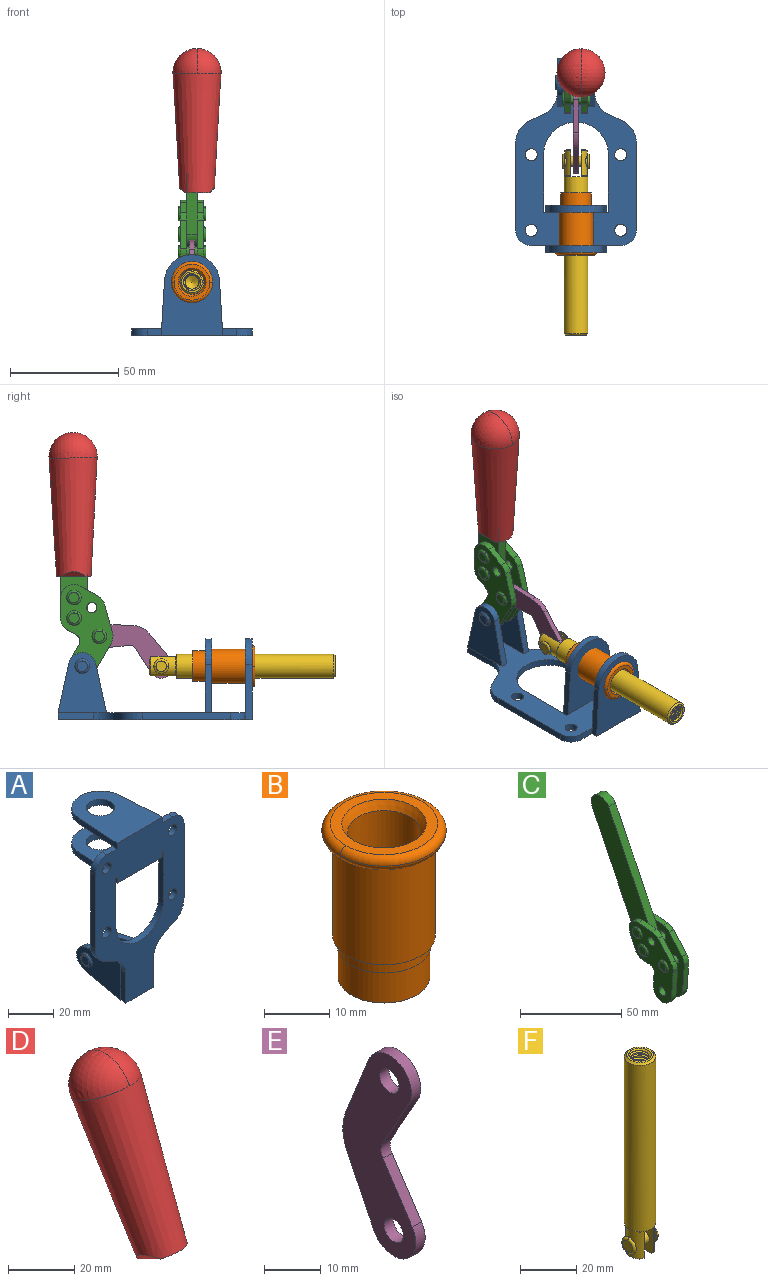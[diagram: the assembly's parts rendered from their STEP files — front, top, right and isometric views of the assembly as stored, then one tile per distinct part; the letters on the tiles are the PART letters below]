
ASSEMBLY  parts=6 mates=6
PART A: 55 faces, bbox 55.7x37.4x89.8 mm
  f0: torus R=2.41mm, axis (-1,0,0), area 15mm2, adj f11,f15,f25
  f1: torus R=2.41mm, axis (-1,0,0), area 15mm2, adj f10,f12,f22
  f2: cylinder r=2.78mm len=5.56mm, axis (0,-1,0), area 54.2mm2, adj f30,f54
  f3: cylinder r=14.99mm len=29.97mm, axis (0,-1,0), area 145.9mm2, adj f30,f49,f53,f54
  f4: cylinder r=2.78mm len=5.56mm, axis (0,-1,0), area 54.2mm2, adj f30,f54
  f5: cylinder r=2.78mm len=5.56mm, axis (0,-1,0), area 54.2mm2, adj f30,f54
  f6: cylinder r=2.78mm len=5.56mm, axis (0,-1,0), area 54.2mm2, adj f30,f54
  f7: cylinder r=6.35mm len=12.7mm, axis (0,0,1), area 123.6mm2, adj f27,f51
  f8: cylinder r=6.35mm len=12.7mm, axis (0,0,-1), area 124.7mm2, adj f21,f35
  f9: cylinder r=2.41mm len=11.18mm, axis (-1,0,0), area 169.4mm2, adj f16,f19
  f10: plane 4.83x4.83mm, normal (1,0,0), area 18.3mm2, adj f1,f12
  f11: plane 4.83x4.83mm, normal (-1,0,0), area 18.3mm2, adj f0,f15
  f12: torus R=2.41mm, axis (-1,0,0), area 15mm2, adj f1,f10,f22
  f13: cylinder r=6.35mm len=12.41mm, axis (1,0,0), area 53.4mm2, adj f18,f19,f22,f23
  f14: cylinder r=6.35mm len=12.41mm, axis (-1,0,0), area 53.4mm2, adj f16,f17,f24,f25
  f15: torus R=2.41mm, axis (-1,0,0), area 15mm2, adj f0,f11,f25
  f16: plane 27.86x22.35mm, normal (1,0,0), area 425.4mm2, adj f9,f14,f17,f24,f30
  f17: plane 22.86x4.97mm, normal (0,0.21,0.98), area 72.5mm2, adj f14,f16,f25,f30
  f18: plane 22.86x4.97mm, normal (0,0.21,0.98), area 72.5mm2, adj f13,f19,f22,f30
  f19: plane 27.86x22.35mm, normal (-1,0,0), area 425.4mm2, adj f9,f13,f18,f23,f30
  f20: cylinder r=12.7mm len=25.35mm, axis (0,0,-1), area 119.8mm2, adj f21,f34,f35,f36
  f21: plane 34.21x28.07mm, normal (0,0,-1), area 702.4mm2, adj f8,f20,f30,f34,f36
  f22: plane 27.96x22.45mm, normal (1,0,0), area 407.2mm2, adj f1,f12,f13,f18,f23,f30,f42,f43
  f23: plane 22.86x4.97mm, normal (0,0.21,-0.98), area 72.5mm2, adj f13,f19,f22,f44
  f24: plane 22.86x4.97mm, normal (0,0.21,-0.98), area 72.5mm2, adj f14,f16,f25,f44
  f25: plane 27.86x22.35mm, normal (-1,0,0), area 407.1mm2, adj f0,f14,f15,f17,f24,f30,f45,f46
  f26: plane 3.1x0.95mm, normal (0,0,-1), area 2.7mm2, adj f30,f49,f50,f54
  f27: plane 34.21x28.07mm, normal (0,0,1), area 702.4mm2, adj f7,f28,f30,f50,f52
  f28: cylinder r=12.7mm len=25.35mm, axis (0,0,1), area 118.8mm2, adj f27,f50,f51,f52
  f29: plane 3.1x0.95mm, normal (0,0,-1), area 2.7mm2, adj f30,f52,f53,f54
  f30: plane 86.54x55.63mm, normal (0,1,0), area 2362.9mm2, adj f2,f3,f4,f5,f6,f16,f17,f18
  f31: plane 40.56x3.1mm, normal (-1,0,0), area 125.7mm2, adj f30,f32,f48,f54
  f32: cylinder r=7.11mm len=7.11mm, axis (0,-1,0), area 34.6mm2, adj f30,f31,f33,f54
  f33: plane 6.67x3.1mm, normal (0,0,1), area 20.4mm2, adj f30,f32,f34,f54
  f34: plane 25.39x3.13mm, normal (-1,0.06,0), area 79.5mm2, adj f20,f21,f33,f35,f54
  f35: plane 37.31x28.45mm, normal (0,0,1), area 789.9mm2, adj f8,f20,f34,f36,f54
  f36: plane 25.39x3.13mm, normal (1,0.06,0), area 79.5mm2, adj f20,f21,f35,f37,f54
  f37: plane 6.67x3.1mm, normal (0,0,1), area 20.4mm2, adj f30,f36,f38,f54
  f38: cylinder r=7.11mm len=7.11mm, axis (0,-1,0), area 34.6mm2, adj f30,f37,f39,f54
  f39: plane 40.56x3.1mm, normal (1,0,0), area 125.7mm2, adj f30,f38,f40,f54
  f40: cylinder r=11.18mm len=10.16mm, axis (0,-1,0), area 39.5mm2, adj f30,f39,f41,f54
  f41: plane 6.09x3.1mm, normal (0.42,0,-0.91), area 20.8mm2, adj f30,f40,f42,f54
  f42: cylinder r=11.18mm len=9.41mm, axis (0,-1,0), area 37.2mm2, adj f22,f30,f41,f43,f54
  f43: plane 16.5x3.1mm, normal (1,0,0), area 51.1mm2, adj f22,f42,f44,f54
  f44: plane 17.37x3.1mm, normal (0,0,-1), area 53.8mm2, adj f23,f24,f30,f43,f45,f54
  f45: plane 16.5x3.1mm, normal (-1,0,0), area 51.1mm2, adj f25,f44,f46,f54
  f46: cylinder r=11.18mm len=9.41mm, axis (0,-1,0), area 37.2mm2, adj f25,f30,f45,f47,f54
  f47: plane 6.09x3.1mm, normal (-0.42,0,-0.91), area 20.8mm2, adj f30,f46,f48,f54
  f48: cylinder r=11.18mm len=10.16mm, axis (0,-1,0), area 39.5mm2, adj f30,f31,f47,f54
  f49: plane 26.54x3.1mm, normal (-1,0,0), area 82.3mm2, adj f3,f26,f30,f54
  f50: plane 25.39x3.1mm, normal (1,0.06,0), area 78.8mm2, adj f26,f27,f28,f51,f54
  f51: plane 37.31x28.45mm, normal (0,0,-1), area 789.9mm2, adj f7,f28,f50,f52,f54
  f52: plane 25.39x3.1mm, normal (-1,0.06,0), area 78.8mm2, adj f27,f28,f29,f51,f54
  f53: plane 26.54x3.1mm, normal (1,0,0), area 82.3mm2, adj f3,f29,f30,f54
  f54: plane 89.66x55.63mm, normal (0,-1,0), area 2678.5mm2, adj f2,f3,f4,f5,f6,f26,f29,f31
PART B: 15 faces, bbox 20.6x20.6x28.7 mm
  f0: torus R=8.26mm, axis (0,0,1), area 56.8mm2, adj f1,f10,f12
  f1: torus R=8.26mm, axis (0,0,1), area 56.8mm2, adj f0,f6,f13
  f2: cylinder r=5.59mm len=25.91mm, axis (0,0,1), area 909.6mm2, adj f3,f4
  f3: cone r=6.86mm half-angle=45deg, axis (0,0,-1), area 70.2mm2, adj f2,f14
  f4: cone r=6.47mm half-angle=30deg, axis (0,0,1), area 66.7mm2, adj f2,f13
  f5: cylinder r=7.04mm len=14.07mm, axis (0,0,1), area 252.6mm2, adj f11,f14
  f6: torus R=8.26mm, axis (0,0,1), area 56.8mm2, adj f1,f12,f13
  f7: cylinder r=7.16mm len=14.33mm, axis (0,0,1), area 91.5mm2, adj f9,f11
  f8: cylinder r=7.86mm len=18.42mm, axis (0,0,1), area 909.6mm2, adj f9,f10
  f9: plane 15.72x15.72mm, normal (0,0,-1), area 33mm2, adj f7,f8
  f10: plane 16.51x16.51mm, normal (0,0,-1), area 19.9mm2, adj f0,f8,f12
  f11: plane 14.33x14.33mm, normal (0,0,-1), area 5.7mm2, adj f5,f7
  f12: torus R=8.26mm, axis (0,0,1), area 56.8mm2, adj f0,f6,f10
  f13: plane 16.51x16.51mm, normal (0,0,1), area 82.7mm2, adj f1,f4,f6
  f14: plane 14.07x14.07mm, normal (0,0,-1), area 7.8mm2, adj f3,f5
PART C: 59 faces, bbox 12.9x60.2x99.6 mm
  f0: torus R=2.39mm, axis (-1,0,0), area 14.9mm2, adj f20,f43,f51
  f1: torus R=2.39mm, axis (-1,0,0), area 14.9mm2, adj f19,f42,f51
  f2: torus R=2.39mm, axis (-1,0,0), area 14.9mm2, adj f18,f35,f51
  f3: torus R=2.39mm, axis (-1,0,0), area 14.9mm2, adj f14,f17,f23
  f4: torus R=2.39mm, axis (-1,0,0), area 14.9mm2, adj f13,f16,f23
  f5: torus R=2.39mm, axis (-1,0,0), area 14.9mm2, adj f12,f15,f23
  f6: cylinder r=2.39mm len=4.78mm, axis (1,0,0), area 46.5mm2, adj f48,f50,f51
  f7: cylinder r=2.39mm len=4.78mm, axis (1,0,0), area 46.5mm2, adj f50,f51
  f8: cylinder r=6.35mm len=12.68mm, axis (1,0,0), area 61.8mm2, adj f38,f39,f50,f51
  f9: cylinder r=2.39mm len=4.78mm, axis (-1,0,0), area 70.5mm2, adj f46,f50
  f10: cylinder r=2.39mm len=4.78mm, axis (-1,0,0), area 46.5mm2, adj f23,f45,f46
  f11: cylinder r=2.39mm len=4.78mm, axis (-1,0,0), area 46.5mm2, adj f23,f46
  f12: plane 4.78x4.78mm, normal (1,0,0), area 17.9mm2, adj f5,f15
  f13: plane 4.78x4.78mm, normal (1,0,0), area 17.9mm2, adj f4,f16
  f14: plane 4.78x4.78mm, normal (1,0,0), area 17.9mm2, adj f3,f17
  f15: torus R=2.39mm, axis (-1,0,0), area 14.9mm2, adj f5,f12,f23
  f16: torus R=2.39mm, axis (-1,0,0), area 14.9mm2, adj f4,f13,f23
  f17: torus R=2.39mm, axis (-1,0,0), area 14.9mm2, adj f3,f14,f23
  f18: plane 4.78x4.78mm, normal (-1,0,0), area 17.9mm2, adj f2,f35
  f19: plane 4.78x4.78mm, normal (-1,0,0), area 17.9mm2, adj f1,f42
  f20: plane 4.78x4.78mm, normal (-1,0,0), area 17.9mm2, adj f0,f43
  f21: plane 2.26x0.2mm, normal (1,0,0), area 0.2mm2, adj f31,f44
  f22: plane 2.26x0.2mm, normal (-1,0,0), area 0.2mm2, adj f41,f44
  f23: plane 39.37x30.77mm, normal (1,0,0), area 565.5mm2, adj f3,f4,f5,f10,f11,f15,f16,f17
  f24: cylinder r=6.1mm len=4.15mm, axis (-1,0,0), area 14.7mm2, adj f23,f25,f32,f46
  f25: plane 10.25x9.01mm, normal (0,-0.75,0.66), area 42.3mm2, adj f23,f24,f26,f46
  f26: cylinder r=6.35mm len=4.64mm, axis (-1,0,0), area 15.6mm2, adj f23,f25,f27,f46
  f27: plane 15.84x3.1mm, normal (0,-1,-0.07), area 49.2mm2, adj f23,f26,f28,f46
  f28: cylinder r=6.35mm len=12.68mm, axis (-1,0,0), area 61.8mm2, adj f23,f27,f29,f46
  f29: plane 8.11x3.1mm, normal (0,1,0.07), area 25.2mm2, adj f23,f28,f30,f46
  f30: cylinder r=3.05mm len=3.25mm, axis (-1,0,0), area 14.8mm2, adj f23,f29,f31,f46
  f31: plane 5.99x3.1mm, normal (0,0.07,-1), area 18.6mm2, adj f21,f23,f30,f44,f46
  f32: plane 9.5x3.1mm, normal (0,-0.07,1), area 29.5mm2, adj f23,f24,f33,f46,f47
  f33: cylinder r=6.1mm len=8.63mm, axis (-1,0,0), area 39.1mm2, adj f23,f32,f34,f47
  f34: plane 8.65x3.96mm, normal (0,0.91,-0.42), area 29.5mm2, adj f23,f33,f44,f47
  f35: torus R=2.39mm, axis (-1,0,0), area 14.9mm2, adj f2,f18,f51
  f36: plane 10.25x9.01mm, normal (0,-0.75,0.66), area 42.3mm2, adj f37,f49,f50,f51
  f37: cylinder r=6.35mm len=4.64mm, axis (1,0,0), area 15.6mm2, adj f36,f38,f50,f51
  f38: plane 15.84x3.1mm, normal (0,-1,-0.07), area 49.2mm2, adj f8,f37,f50,f51
  f39: plane 8.11x3.1mm, normal (0,1,0.07), area 25.2mm2, adj f8,f40,f50,f51
  f40: cylinder r=3.05mm len=3.25mm, axis (1,0,0), area 14.8mm2, adj f39,f41,f50,f51
  f41: plane 5.99x3.1mm, normal (0,0.07,-1), area 18.6mm2, adj f22,f40,f44,f50,f51
  f42: torus R=2.39mm, axis (-1,0,0), area 14.9mm2, adj f1,f19,f51
  f43: torus R=2.39mm, axis (-1,0,0), area 14.9mm2, adj f0,f20,f51
  f44: cylinder r=6.35mm len=12.12mm, axis (-1,0,0), area 128.9mm2, adj f21,f22,f23,f31,f34,f41,f46,f47
  f45: plane 2.65x1.35mm, normal (1,0,0), area 1mm2, adj f10,f55
  f46: plane 39.08x20.42mm, normal (-1,0,0), area 412.5mm2, adj f9,f10,f11,f24,f25,f26,f27,f28
  f47: plane 77.62x39.82mm, normal (1,0,0), area 850mm2, adj f32,f33,f34,f44,f53,f54,f55
  f48: plane 2.65x1.35mm, normal (-1,0,0), area 1mm2, adj f6,f55
  f49: cylinder r=6.1mm len=4.15mm, axis (1,0,0), area 14.7mm2, adj f36,f50,f51,f56
  f50: plane 39.08x20.42mm, normal (1,0,0), area 412.5mm2, adj f6,f7,f8,f9,f36,f37,f38,f39
  f51: plane 39.37x30.77mm, normal (-1,0,0), area 565.5mm2, adj f0,f1,f2,f6,f7,f8,f35,f36
  f52: plane 8.65x3.96mm, normal (0,0.91,-0.42), area 29.5mm2, adj f44,f51,f57,f58
  f53: plane 68.49x33.4mm, normal (0,0.9,-0.44), area 358.1mm2, adj f44,f47,f54,f58
  f54: cylinder r=6.35mm len=12.06mm, axis (1,0,0), area 93.7mm2, adj f47,f53,f55,f58
  f55: plane 68.49x33.4mm, normal (0,-0.9,0.44), area 358.1mm2, adj f44,f45,f46,f47,f48,f50,f54,f58
  f56: plane 9.5x3.1mm, normal (0,-0.07,1), area 29.5mm2, adj f49,f50,f51,f57,f58
  f57: cylinder r=6.1mm len=8.63mm, axis (1,0,0), area 39.1mm2, adj f51,f52,f56,f58
  f58: plane 77.62x39.82mm, normal (-1,0,0), area 850mm2, adj f44,f52,f53,f54,f55,f56,f57
PART D: 11 faces, bbox 22.3x42.6x64.5 mm
  f0: sphere r=11.13mm, area 411.4mm2, adj f1,f8
  f1: cone r=11.11mm half-angle=3.3deg, axis (0,0.44,0.9), area 3251.8mm2, adj f0,f7,f8,f9,f10
  f2: cylinder r=6.16mm len=11.7mm, axis (1,0,0), area 89.5mm2, adj f3,f4,f5,f6
  f3: plane 60.23x36.75mm, normal (-1,0,0), area 763.6mm2, adj f2,f4,f6,f10
  f4: plane 51.37x25.05mm, normal (0,0.9,-0.44), area 264.2mm2, adj f2,f3,f5,f10
  f5: plane 60.23x36.75mm, normal (1,0,0), area 763.6mm2, adj f2,f4,f6,f10
  f6: plane 51.37x25.05mm, normal (0,-0.9,0.44), area 264.2mm2, adj f2,f3,f5,f10
  f7: plane 9.95x5.95mm, normal (0.71,-0.31,-0.64), area 25.8mm2, adj f1,f10
  f8: sphere r=11.13mm, area 411.4mm2, adj f0,f1
  f9: plane 9.95x5.95mm, normal (-0.71,-0.31,-0.64), area 25.8mm2, adj f1,f10
  f10: plane 14.27x11.38mm, normal (0,-0.44,-0.9), area 106.7mm2, adj f1,f3,f4,f5,f6,f7,f9
PART E: 12 faces, bbox 2.3x18.2x42.8 mm
  f0: cylinder r=2.4mm len=4.8mm, axis (1,0,0), area 34.9mm2, adj f4,f11
  f1: cylinder r=10.41mm len=8.47mm, axis (1,0,0), area 20.2mm2, adj f4,f9,f10,f11
  f2: cylinder r=3.05mm len=3.16mm, axis (1,0,0), area 7.7mm2, adj f4,f6,f7,f11
  f3: cylinder r=2.4mm len=4.8mm, axis (1,0,0), area 34.9mm2, adj f4,f11
  f4: plane 42.81x18.23mm, normal (-1,0,0), area 414.1mm2, adj f0,f1,f2,f3,f5,f6,f7,f8
  f5: cylinder r=5.54mm len=10.67mm, axis (1,0,0), area 41.8mm2, adj f4,f6,f10,f11
  f6: plane 11.66x6.53mm, normal (0,-0.87,-0.49), area 30.9mm2, adj f2,f4,f5,f11
  f7: plane 11.17x7.33mm, normal (0,-0.84,0.55), area 30.9mm2, adj f2,f4,f8,f11
  f8: cylinder r=5.54mm len=10.51mm, axis (1,0,0), area 41.8mm2, adj f4,f7,f9,f11
  f9: plane 13.67x6.67mm, normal (0,0.9,-0.44), area 35.1mm2, adj f1,f4,f8,f11
  f10: plane 14.1x5.7mm, normal (0,0.93,0.37), area 35.1mm2, adj f1,f4,f5,f11
  f11: plane 42.81x18.23mm, normal (1,0,0), area 414.1mm2, adj f0,f1,f2,f3,f5,f6,f7,f8
PART F: 48 faces, bbox 12.6x11.1x86.1 mm
  f0: torus R=2.41mm, axis (-1,0,0), area 15mm2, adj f30,f32,f34
  f1: torus R=2.41mm, axis (-1,0,0), area 15mm2, adj f29,f31,f33
  f2: cylinder r=5.54mm len=72.39mm, axis (0,0,1), area 2518.5mm2, adj f3,f4,f42,f43
  f3: cone r=5.54mm half-angle=45deg, axis (0,0,1), area 7.6mm2, adj f2,f5,f41
  f4: cone r=5.54mm half-angle=45deg, axis (0,0,-1), area 34.9mm2, adj f2,f39
  f5: cylinder r=5.08mm len=11.48mm, axis (0,0,1), area 108.3mm2, adj f3,f7,f8,f41
  f6: cylinder r=2.41mm len=4.83mm, axis (-1,0,0), area 71.2mm2, adj f40,f41
  f7: cylinder r=2.41mm len=4.83mm, axis (-1,0,0), area 7.6mm2, adj f5,f34
  f8: cone r=5.08mm half-angle=45deg, axis (0,0,1), area 10.6mm2, adj f5,f37,f41
  f9: cone r=3.98mm half-angle=45deg, axis (0,0,1), area 17.6mm2, adj f27,f39,f45,f46,f47
  f10: cylinder r=2.41mm len=4.83mm, axis (-1,0,0), area 7.6mm2, adj f33,f38
  f11: cylinder r=3.2mm len=6.4mm, axis (0,0,1), area 78.4mm2, adj f12,f28,f44,f45,f47
  f12: cylinder r=3.2mm len=6.4mm, axis (0,0,1), area 10.5mm2, adj f11,f13,f45,f47
  f13: cylinder r=3.2mm len=6.4mm, axis (0,0,1), area 10.5mm2, adj f12,f14,f45,f47
  f14: cylinder r=3.2mm len=6.4mm, axis (0,0,1), area 10.5mm2, adj f13,f15,f45,f47
  f15: cylinder r=3.2mm len=6.4mm, axis (0,0,1), area 10.5mm2, adj f14,f16,f45,f47
  f16: cylinder r=3.2mm len=6.4mm, axis (0,0,1), area 10.5mm2, adj f15,f17,f45,f47
  f17: cylinder r=3.2mm len=6.4mm, axis (0,0,1), area 10.5mm2, adj f16,f18,f45,f47
  f18: cylinder r=3.2mm len=6.4mm, axis (0,0,1), area 10.5mm2, adj f17,f19,f45,f47
  f19: cylinder r=3.2mm len=6.4mm, axis (0,0,1), area 10.5mm2, adj f18,f20,f45,f47
  f20: cylinder r=3.2mm len=6.4mm, axis (0,0,1), area 10.5mm2, adj f19,f21,f45,f47
  f21: cylinder r=3.2mm len=6.4mm, axis (0,0,1), area 10.5mm2, adj f20,f22,f45,f47
  f22: cylinder r=3.2mm len=6.4mm, axis (0,0,1), area 10.5mm2, adj f21,f23,f45,f47
  f23: cylinder r=3.2mm len=6.4mm, axis (0,0,1), area 10.5mm2, adj f22,f24,f45,f47
  f24: cylinder r=3.2mm len=6.4mm, axis (0,0,1), area 10.5mm2, adj f23,f25,f45,f47
  f25: cylinder r=3.2mm len=6.4mm, axis (0,0,1), area 10.5mm2, adj f24,f26,f45,f47
  f26: cylinder r=3.2mm len=6.4mm, axis (0,0,1), area 10.5mm2, adj f25,f27,f45,f47
  f27: cylinder r=3.2mm len=6.4mm, axis (0,0,1), area 7.4mm2, adj f9,f26,f45,f47
  f28: cone r=3.2mm half-angle=60deg, axis (0,0,1), area 37.2mm2, adj f11
  f29: plane 4.83x4.83mm, normal (-1,0,0), area 18.3mm2, adj f1,f31
  f30: plane 4.83x4.83mm, normal (1,0,0), area 18.3mm2, adj f0,f32
  f31: torus R=2.41mm, axis (-1,0,0), area 15mm2, adj f1,f29,f33
  f32: torus R=2.41mm, axis (-1,0,0), area 15mm2, adj f0,f30,f34
  f33: plane 6.83x6.83mm, normal (1,0,0), area 18.3mm2, adj f1,f10,f31
  f34: plane 6.83x6.83mm, normal (-1,0,0), area 18.3mm2, adj f0,f7,f32
  f35: cone r=5.08mm half-angle=45deg, axis (0,0,1), area 10.6mm2, adj f36,f38,f40
  f36: plane 7.25x1.97mm, normal (0,0,-1), area 10mm2, adj f35,f40
  f37: plane 7.25x1.97mm, normal (0,0,-1), area 10mm2, adj f8,f41
  f38: cylinder r=5.08mm len=11.48mm, axis (0,0,1), area 108.3mm2, adj f10,f35,f40,f42
  f39: plane 9.55x9.55mm, normal (0,0,1), area 22mm2, adj f4,f9
  f40: plane 12.76x10.09mm, normal (1,0,0), area 95.7mm2, adj f6,f35,f36,f38,f42,f43
  f41: plane 12.76x10.09mm, normal (-1,0,0), area 95.7mm2, adj f3,f5,f6,f8,f37,f43
  f42: cone r=5.54mm half-angle=45deg, axis (0,0,1), area 7.6mm2, adj f2,f38,f40
  f43: plane 11.07x4.7mm, normal (0,0,-1), area 50.4mm2, adj f2,f40,f41
  f44: plane 0.89x0.62mm, normal (-1,0,0), area 0.3mm2, adj f11,f45,f46,f47
  f45: bspline ~24.8x7.63mm, area 266.6mm2, adj f9,f11,f12,f13,f14,f15,f16,f17
  f46: bspline ~24.87x7.63mm, area 73.6mm2, adj f9,f44,f45,f47
  f47: bspline ~24.98x7.63mm, area 272.5mm2, adj f9,f11,f12,f13,f14,f15,f16,f17
PLACE A rot(axis=(1,0,0),90deg) t=(0,1.23,-3.1)mm fixed
PLACE B rot(axis=(1,0,0),90deg) t=(0,2.5,-3.1)mm
PLACE C rot(axis=(1,0,0),25.7deg) t=(0,-2.75,39.79)mm
PLACE D rot(axis=(1,0,0),25.7deg) t=(2.31,-2.75,39.79)mm
PLACE E rot(axis=(1,0,0),117.8deg) t=(0,22.03,6.94)mm
PLACE F rot(axis=(1,0,0),90deg) t=(0,12.35,-3.1)mm
MATE fastened A.f7 <-> B.f2  axis (0,-1,0) through (0,-45.16,21.51)mm
MATE revolute E.f5 <-> F.f6  axis (1,0,0) through (0,-3.12,21.51)mm
MATE revolute E.f3 <-> C.f4  axis (1,0,0) through (0,25.47,35.31)mm
MATE fastened B.f12 <-> F.f2  axis (0,-1,0) through (0,-46.43,21.51)mm
MATE fastened D.f2 <-> C.f54  axis (1,0,0) through (0,37.57,119.92)mm
MATE revolute C.f7 <-> A.f0  axis (1,0,0) through (0,33.32,21.51)mm
